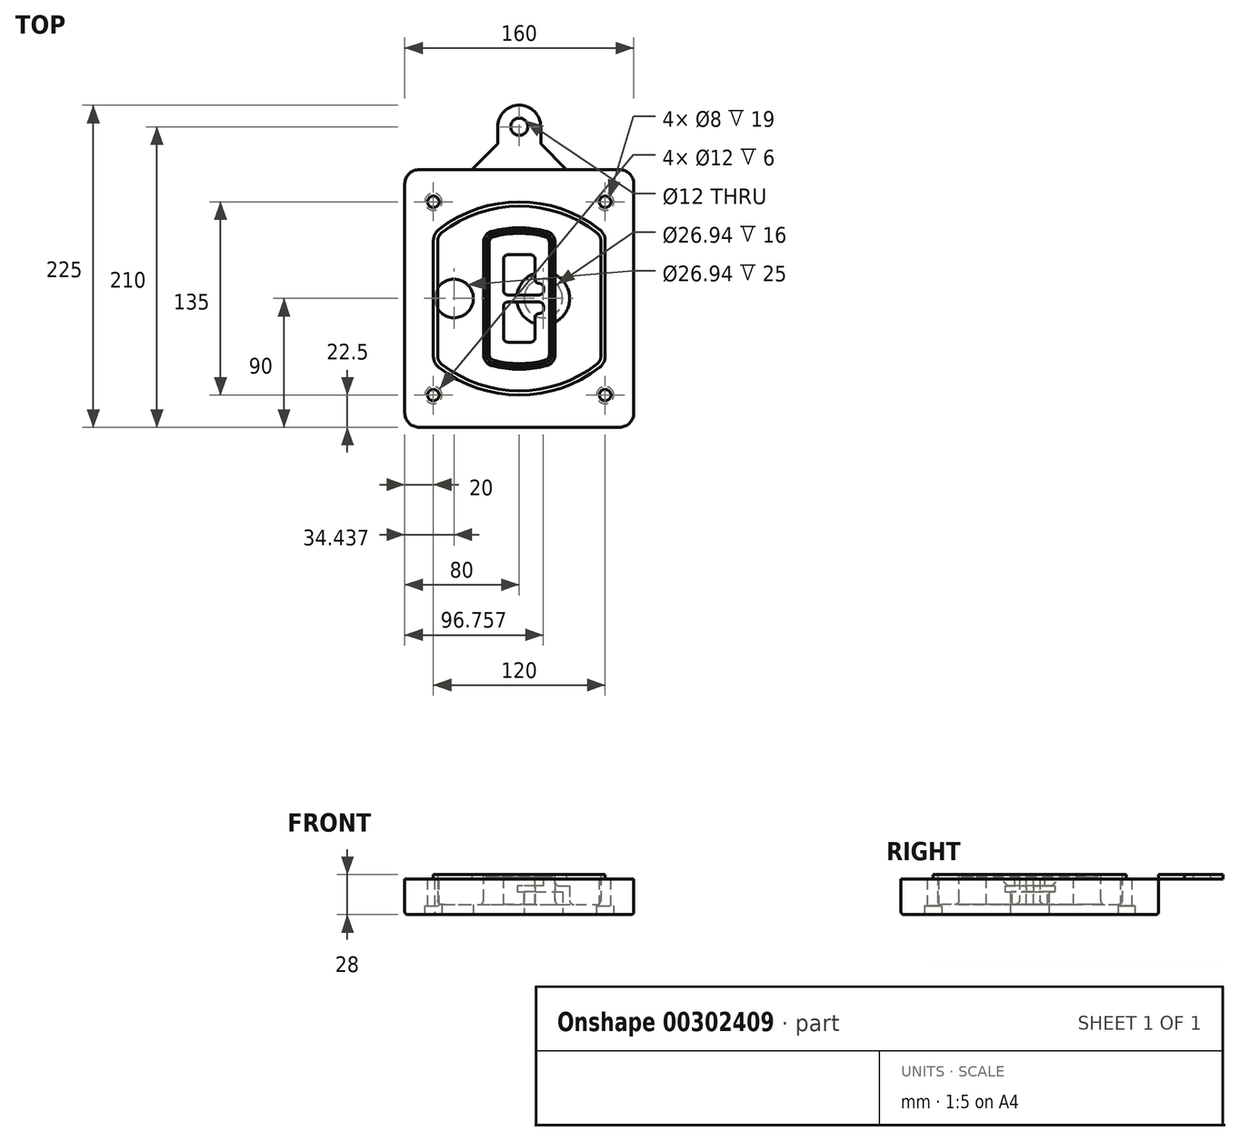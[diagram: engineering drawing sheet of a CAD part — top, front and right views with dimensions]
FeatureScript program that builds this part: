
annotation { "Feature Type Name" : "Feature", "Feature Type Description" : "" }
export const myFeature = defineFeature(function(context is Context, id is Id, definition is map)
    precondition{}
    {
        {
            var Q0;
            Q0=qCreatedBy(makeId("Top.planeOp"),FACE);
            var sketch = newSketch(context, id + "F0", { "sketchPlane" : qUnion([Q0])});
            skPoint(sketch, "E0.rect.middle", {"position": v(0, 0) * mm});
            skLineSegment(sketch, "E1.bottom", {"start": v(-70, -90) * mm, "end": v(70, -90) * mm});
            skLineSegment(sketch, "E1.top", {"start": v(-70, 90) * mm, "end": v(70, 90) * mm});
            skLineSegment(sketch, "E1.left", {"start": v(-80, -80) * mm, "end": v(-80, 80) * mm});
            skLineSegment(sketch, "E1.right", {"start": v(80, -80) * mm, "end": v(80, 80) * mm});
            skLineSegment(sketch, "E2", {"start": v(-80, 90) * mm, "end": v(80, -90) * mm, "construction": true});
            skLineSegment(sketch, "E3", {"start": v(80, 90) * mm, "end": v(-80, -90) * mm, "construction": true});
            skCircle(sketch, "E4", {"center": v(-60, 67.5) * mm, "radius": 4 * mm});
            skCircle(sketch, "E5", {"center": v(60, 67.5) * mm, "radius": 4 * mm});
            skCircle(sketch, "E6", {"center": v(60, -67.5) * mm, "radius": 4 * mm});
            skCircle(sketch, "E7", {"center": v(-60, -67.5) * mm, "radius": 4 * mm});
            skLineSegment(sketch, "E8", {"start": v(-60, 67.5) * mm, "end": v(60, 67.5) * mm, "construction": true});
            skLineSegment(sketch, "E9", {"start": v(60, 67.5) * mm, "end": v(60, -67.5) * mm, "construction": true});
            skLineSegment(sketch, "E10", {"start": v(60, -67.5) * mm, "end": v(-60, -67.5) * mm, "construction": true});
            skLineSegment(sketch, "E11", {"start": v(-60, -67.5) * mm, "end": v(-60, 67.5) * mm, "construction": true});
            skLineSegment(sketch, "E12", {"start": v(-60, 40.3) * mm, "end": v(-60, -40.3) * mm});
            skLineSegment(sketch, "E13", {"start": v(60, 40.3) * mm, "end": v(60, -40.3) * mm});
            skArc(sketch, "E14", {"start": v(56.15, 48.18) * mm, "mid": v(0, 67.5) * mm, "end": v(-56.15, 48.18) * mm});
            skArc(sketch, "E15", {"start": v(-56.15, -48.18) * mm, "mid": v(0, -67.5) * mm, "end": v(56.15, -48.18) * mm});
            skLineSegment(sketch, "E16", {"start": v(-60, 0) * mm, "end": v(60, 0) * mm, "construction": true});
            skPoint(sketch, "E17.visualSharp", {"position": v(-60, -45) * mm});
            skArc(sketch, "E17.filletArc", {"start": v(-60, -40.3) * mm, "mid": v(-58.99, -44.68) * mm, "end": v(-56.15, -48.18) * mm});
            skPoint(sketch, "E18.visualSharp", {"position": v(-60, 45) * mm});
            skArc(sketch, "E18.filletArc", {"start": v(-56.15, 48.18) * mm, "mid": v(-58.99, 44.68) * mm, "end": v(-60, 40.3) * mm});
            skPoint(sketch, "E19.visualSharp", {"position": v(60, 45) * mm});
            skArc(sketch, "E19.filletArc", {"start": v(60, 40.3) * mm, "mid": v(58.99, 44.68) * mm, "end": v(56.15, 48.18) * mm});
            skPoint(sketch, "E20.visualSharp", {"position": v(60, -45) * mm});
            skArc(sketch, "E20.filletArc", {"start": v(56.15, -48.18) * mm, "mid": v(58.99, -44.68) * mm, "end": v(60, -40.3) * mm});
            skPoint(sketch, "E21.visualSharp", {"position": v(-80, 90) * mm});
            skArc(sketch, "E21.filletArc", {"start": v(-70, 90) * mm, "mid": v(-77.07, 87.07) * mm, "end": v(-80, 80) * mm});
            skPoint(sketch, "E22.visualSharp", {"position": v(80, 90) * mm});
            skArc(sketch, "E22.filletArc", {"start": v(80, 80) * mm, "mid": v(77.07, 87.07) * mm, "end": v(70, 90) * mm});
            skPoint(sketch, "E23.visualSharp", {"position": v(80, -90) * mm});
            skArc(sketch, "E23.filletArc", {"start": v(70, -90) * mm, "mid": v(77.07, -87.07) * mm, "end": v(80, -80) * mm});
            skPoint(sketch, "E24.visualSharp", {"position": v(-80, -90) * mm});
            skArc(sketch, "E24.filletArc", {"start": v(-80, -80) * mm, "mid": v(-77.07, -87.07) * mm, "end": v(-70, -90) * mm});
            skArc(sketch, "E25.0", {"start": v(57, 40.3) * mm, "mid": v(56.3, 43.36) * mm, "end": v(54.3, 45.81) * mm});
            skLineSegment(sketch, "E25.1", {"start": v(57, 40.3) * mm, "end": v(57, -40.3) * mm});
            skArc(sketch, "E25.2", {"start": v(54.3, -45.81) * mm, "mid": v(56.3, -43.36) * mm, "end": v(57, -40.3) * mm});
            skArc(sketch, "E25.3", {"start": v(-54.3, -45.81) * mm, "mid": v(0, -64.5) * mm, "end": v(54.3, -45.81) * mm});
            skArc(sketch, "E25.4", {"start": v(-57, -40.3) * mm, "mid": v(-56.3, -43.36) * mm, "end": v(-54.3, -45.81) * mm});
            skArc(sketch, "E25.5", {"start": v(54.3, 45.81) * mm, "mid": v(0, 64.5) * mm, "end": v(-54.3, 45.81) * mm});
            skLineSegment(sketch, "E25.6", {"start": v(-57, 40.3) * mm, "end": v(-57, -40.3) * mm});
            skArc(sketch, "E25.7", {"start": v(-54.3, 45.81) * mm, "mid": v(-56.3, 43.36) * mm, "end": v(-57, 40.3) * mm});
            skArc(sketch, "E26.0", {"start": v(-58.62, 51.33) * mm, "mid": v(-62.58, 46.43) * mm, "end": v(-64, 40.3) * mm});
            skArc(sketch, "E26.1", {"start": v(58.62, 51.33) * mm, "mid": v(0, 71.5) * mm, "end": v(-58.62, 51.33) * mm});
            skArc(sketch, "E26.2", {"start": v(64, 40.3) * mm, "mid": v(62.58, 46.43) * mm, "end": v(58.62, 51.33) * mm});
            skLineSegment(sketch, "E26.3", {"start": v(64, 40.3) * mm, "end": v(64, -40.3) * mm});
            skArc(sketch, "E26.4", {"start": v(58.62, -51.33) * mm, "mid": v(62.58, -46.43) * mm, "end": v(64, -40.3) * mm});
            skLineSegment(sketch, "E26.5", {"start": v(-64, 40.3) * mm, "end": v(-64, -40.3) * mm});
            skArc(sketch, "E26.6", {"start": v(-58.62, -51.33) * mm, "mid": v(0, -71.5) * mm, "end": v(58.62, -51.33) * mm});
            skArc(sketch, "E26.7", {"start": v(-64, -40.3) * mm, "mid": v(-62.58, -46.43) * mm, "end": v(-58.62, -51.33) * mm});
            skSolve(sketch);
        }
        {
            var Q0;
            Q0=makeQuery(id+"F0.imprint","IMPRINT",FACE,{"disambiguationData":[TD([[makeQuery(id+"F0.imprint","IMPRINT",EDGE,{"derivedFrom":sQuery(id+"F0.wireOp",EDGE,"E1.bottom")}),1.0]])]});
            var Q1;
            Q1=makeQuery(id+"F0.imprint","IMPRINT",FACE,{"disambiguationData":[TD([[makeQuery(id+"F0.imprint","IMPRINT",EDGE,{"derivedFrom":sQuery(id+"F0.wireOp",EDGE,"E12")}),1.0]])]});
            var Q2;
            Q2=makeQuery(id+"F0.imprint","IMPRINT",FACE,{"disambiguationData":[TD([[makeQuery(id+"F0.imprint","IMPRINT",EDGE,{"derivedFrom":sQuery(id+"F0.wireOp",EDGE,"E25.0")}),1.0]])]});
            var Q3;
            Q3=makeQuery(id+"F0.imprint","IMPRINT",FACE,{"disambiguationData":[TD([[makeQuery(id+"F0.imprint","IMPRINT",EDGE,{"derivedFrom":sQuery(id+"F0.wireOp",EDGE,"E12")}),-1.0]])]});
            extrude(context, id + "F1", {"entities" : qUnion([Q0, Q1, Q2, Q3]), "oppositeDirection" : true, "depth" : 25 * mm});
        }
        {
            var Q0;
            Q0=makeQuery(id+"F0.imprint","IMPRINT",FACE,{"disambiguationData":[TD([[makeQuery(id+"F0.imprint","IMPRINT",EDGE,{"derivedFrom":sQuery(id+"F0.wireOp",EDGE,"E12")}),1.0]])]});
            extrude(context, id + "F2", {"entities" : qUnion([Q0]), "operationType" : NewBodyOperationType.ADD, "depth" : 3 * mm});
        }
        {
            var Q0;
            Q0=makeQuery(id+"F0.imprint","IMPRINT",FACE,{"disambiguationData":[TD([[makeQuery(id+"F0.imprint","IMPRINT",EDGE,{"derivedFrom":sQuery(id+"F0.wireOp",EDGE,"E25.0")}),1.0]])]});
            extrude(context, id + "F3", {"entities" : qUnion([Q0]), "operationType" : NewBodyOperationType.REMOVE, "oppositeDirection" : true, "depth" : 18 * mm});
        }
        {
            var Q0;
            Q0=makeQuery(id+"F2.opExtrude","CAP_FACE",FACE,{"disambiguationData":[OSD([sQuery(id+"F0.wireOp",EDGE,"E12"),sQuery(id+"F0.wireOp",EDGE,"E13"),sQuery(id+"F0.wireOp",EDGE,"E14"),sQuery(id+"F0.wireOp",EDGE,"E15"),sQuery(id+"F0.wireOp",EDGE,"E17.filletArc"),sQuery(id+"F0.wireOp",EDGE,"E18.filletArc"),sQuery(id+"F0.wireOp",EDGE,"E19.filletArc"),sQuery(id+"F0.wireOp",EDGE,"E20.filletArc"),sQuery(id+"F0.wireOp",EDGE,"E25.0"),sQuery(id+"F0.wireOp",EDGE,"E25.1"),sQuery(id+"F0.wireOp",EDGE,"E25.2"),sQuery(id+"F0.wireOp",EDGE,"E25.3"),sQuery(id+"F0.wireOp",EDGE,"E25.4"),sQuery(id+"F0.wireOp",EDGE,"E25.5"),sQuery(id+"F0.wireOp",EDGE,"E25.6"),sQuery(id+"F0.wireOp",EDGE,"E25.7")])],"isStart":false});
            var sketch = newSketch(context, id + "F4", { "sketchPlane" : qUnion([Q0])});
            skArc(sketch, "E27.0", {"start": v(-19.08, -46.97) * mm, "mid": v(0, -49.5) * mm, "end": v(19.08, -46.97) * mm});
            skArc(sketch, "E28.0", {"start": v(19.08, 46.97) * mm, "mid": v(0, 49.5) * mm, "end": v(-19.08, 46.97) * mm});
            skLineSegment(sketch, "E29", {"start": v(-25, 39.25) * mm, "end": v(-25, -39.25) * mm});
            skLineSegment(sketch, "E30", {"start": v(25, 39.25) * mm, "end": v(25, -39.25) * mm});
            skLineSegment(sketch, "E31", {"start": v(-25, 45.1) * mm, "end": v(25, 45.1) * mm, "construction": true});
            skLineSegment(sketch, "E32", {"start": v(-25, -45.1) * mm, "end": v(25, -45.1) * mm, "construction": true});
            skPoint(sketch, "E33.visualSharp", {"position": v(-25, 45.1) * mm});
            skArc(sketch, "E33.filletArc", {"start": v(-19.08, 46.97) * mm, "mid": v(-23.35, 44.11) * mm, "end": v(-25, 39.25) * mm});
            skPoint(sketch, "E34.visualSharp", {"position": v(25, 45.1) * mm});
            skArc(sketch, "E34.filletArc", {"start": v(25, 39.25) * mm, "mid": v(23.35, 44.11) * mm, "end": v(19.08, 46.97) * mm});
            skPoint(sketch, "E35.visualSharp", {"position": v(25, -45.1) * mm});
            skArc(sketch, "E35.filletArc", {"start": v(19.08, -46.97) * mm, "mid": v(23.35, -44.11) * mm, "end": v(25, -39.25) * mm});
            skPoint(sketch, "E36.visualSharp", {"position": v(-25, -45.1) * mm});
            skArc(sketch, "E36.filletArc", {"start": v(-25, -39.25) * mm, "mid": v(-23.35, -44.11) * mm, "end": v(-19.08, -46.97) * mm});
            skArc(sketch, "E37.0", {"start": v(54.3, 45.81) * mm, "mid": v(0, 64.5) * mm, "end": v(-54.3, 45.81) * mm});
            skArc(sketch, "E37.1", {"start": v(-54.3, 45.81) * mm, "mid": v(-56.3, 43.36) * mm, "end": v(-57, 40.3) * mm});
            skLineSegment(sketch, "E37.2", {"start": v(-57, 40.3) * mm, "end": v(-57, -40.3) * mm});
            skArc(sketch, "E37.3", {"start": v(-57, -40.3) * mm, "mid": v(-56.3, -43.36) * mm, "end": v(-54.3, -45.81) * mm});
            skArc(sketch, "E37.4", {"start": v(-54.3, -45.81) * mm, "mid": v(0, -64.5) * mm, "end": v(54.3, -45.81) * mm});
            skArc(sketch, "E37.5", {"start": v(54.3, -45.81) * mm, "mid": v(56.3, -43.36) * mm, "end": v(57, -40.3) * mm});
            skLineSegment(sketch, "E37.6", {"start": v(57, 40.3) * mm, "end": v(57, -40.3) * mm});
            skArc(sketch, "E37.7", {"start": v(57, 40.3) * mm, "mid": v(56.3, 43.36) * mm, "end": v(54.3, 45.81) * mm});
            skLineSegment(sketch, "E38.0", {"start": v(23, 39.25) * mm, "end": v(23, -39.25) * mm});
            skArc(sketch, "E38.1", {"start": v(18.56, -45.04) * mm, "mid": v(21.76, -42.9) * mm, "end": v(23, -39.25) * mm});
            skArc(sketch, "E38.2", {"start": v(-18.56, -45.04) * mm, "mid": v(0, -47.5) * mm, "end": v(18.56, -45.04) * mm});
            skArc(sketch, "E38.3", {"start": v(-23, -39.25) * mm, "mid": v(-21.76, -42.9) * mm, "end": v(-18.56, -45.04) * mm});
            skLineSegment(sketch, "E38.4", {"start": v(-23, 39.25) * mm, "end": v(-23, -39.25) * mm});
            skArc(sketch, "E38.5", {"start": v(23, 39.25) * mm, "mid": v(21.76, 42.9) * mm, "end": v(18.56, 45.04) * mm});
            skArc(sketch, "E38.6", {"start": v(-18.56, 45.04) * mm, "mid": v(-21.76, 42.9) * mm, "end": v(-23, 39.25) * mm});
            skArc(sketch, "E38.7", {"start": v(18.56, 45.04) * mm, "mid": v(0, 47.5) * mm, "end": v(-18.56, 45.04) * mm});
            skArc(sketch, "E39.0", {"start": v(21, 39.25) * mm, "mid": v(20.18, 41.68) * mm, "end": v(18.04, 43.1) * mm});
            skLineSegment(sketch, "E39.1", {"start": v(21, 39.25) * mm, "end": v(21, -39.25) * mm});
            skArc(sketch, "E39.2", {"start": v(18.04, -43.1) * mm, "mid": v(20.18, -41.68) * mm, "end": v(21, -39.25) * mm});
            skArc(sketch, "E39.3", {"start": v(-18.04, -43.1) * mm, "mid": v(0, -45.5) * mm, "end": v(18.04, -43.1) * mm});
            skArc(sketch, "E39.4", {"start": v(-21, -39.25) * mm, "mid": v(-20.18, -41.68) * mm, "end": v(-18.04, -43.1) * mm});
            skArc(sketch, "E39.5", {"start": v(18.04, 43.1) * mm, "mid": v(0, 45.5) * mm, "end": v(-18.04, 43.1) * mm});
            skLineSegment(sketch, "E39.6", {"start": v(-21, 39.25) * mm, "end": v(-21, -39.25) * mm});
            skArc(sketch, "E39.7", {"start": v(-18.04, 43.1) * mm, "mid": v(-20.18, 41.68) * mm, "end": v(-21, 39.25) * mm});
            skLineSegment(sketch, "E40", {"start": v(-25, 0) * mm, "end": v(25, 0) * mm, "construction": true});
            skLineSegment(sketch, "E41", {"start": v(-11, 5.5) * mm, "end": v(-11, 27.5) * mm});
            skLineSegment(sketch, "E42", {"start": v(-8, 30.5) * mm, "end": v(8, 30.5) * mm});
            skLineSegment(sketch, "E43", {"start": v(11, 27.5) * mm, "end": v(11, 13.5) * mm});
            skLineSegment(sketch, "E44", {"start": v(14, 10.5) * mm, "end": v(14, 10.5) * mm});
            skLineSegment(sketch, "E45", {"start": v(17, 7.5) * mm, "end": v(17, 5.5) * mm});
            skLineSegment(sketch, "E46", {"start": v(14, 2.5) * mm, "end": v(-8, 2.5) * mm});
            skPoint(sketch, "E47.visualSharp", {"position": v(-11, 30.5) * mm});
            skArc(sketch, "E47.filletArc", {"start": v(-8, 30.5) * mm, "mid": v(-10.12, 29.62) * mm, "end": v(-11, 27.5) * mm});
            skPoint(sketch, "E48.visualSharp", {"position": v(11, 30.5) * mm});
            skArc(sketch, "E48.filletArc", {"start": v(11, 27.5) * mm, "mid": v(10.12, 29.62) * mm, "end": v(8, 30.5) * mm});
            skPoint(sketch, "E49.visualSharp", {"position": v(11, 10.5) * mm});
            skArc(sketch, "E49.filletArc", {"start": v(11, 13.5) * mm, "mid": v(11.88, 11.38) * mm, "end": v(14, 10.5) * mm});
            skPoint(sketch, "E50.visualSharp", {"position": v(17, 10.5) * mm});
            skArc(sketch, "E50.filletArc", {"start": v(17, 7.5) * mm, "mid": v(16.12, 9.62) * mm, "end": v(14, 10.5) * mm});
            skPoint(sketch, "E51.visualSharp", {"position": v(17, 2.5) * mm});
            skArc(sketch, "E51.filletArc", {"start": v(14, 2.5) * mm, "mid": v(16.12, 3.38) * mm, "end": v(17, 5.5) * mm});
            skPoint(sketch, "E52.visualSharp", {"position": v(-11, 2.5) * mm});
            skArc(sketch, "E52.filletArc", {"start": v(-11, 5.5) * mm, "mid": v(-10.12, 3.38) * mm, "end": v(-8, 2.5) * mm});
            skLineSegment(sketch, "E53.0.MirrorCS", {"start": v(14, -2.5) * mm, "end": v(-8, -2.5) * mm});
            skArc(sketch, "E54.0.MirrorCS", {"start": v(-11, -5.5) * mm, "mid": v(-10.12, -3.38) * mm, "end": v(-8, -2.5) * mm});
            skLineSegment(sketch, "E55.0.MirrorCS", {"start": v(-11, -5.5) * mm, "end": v(-11, -27.5) * mm});
            skArc(sketch, "E56.0.MirrorCS", {"start": v(-8, -30.5) * mm, "mid": v(-10.12, -29.62) * mm, "end": v(-11, -27.5) * mm});
            skLineSegment(sketch, "E57.0.MirrorCS", {"start": v(-8, -30.5) * mm, "end": v(8, -30.5) * mm});
            skArc(sketch, "E58.0.MirrorCS", {"start": v(11, -27.5) * mm, "mid": v(10.12, -29.62) * mm, "end": v(8, -30.5) * mm});
            skLineSegment(sketch, "E59.0.MirrorCS", {"start": v(11, -27.5) * mm, "end": v(11, -13.5) * mm});
            skArc(sketch, "E60.0.MirrorCS", {"start": v(11, -13.5) * mm, "mid": v(11.88, -11.38) * mm, "end": v(14, -10.5) * mm});
            skArc(sketch, "E61.0.MirrorCS", {"start": v(17, -7.5) * mm, "mid": v(16.12, -9.62) * mm, "end": v(14, -10.5) * mm});
            skLineSegment(sketch, "E62.0.MirrorCS", {"start": v(17, -7.5) * mm, "end": v(17, -5.5) * mm});
            skArc(sketch, "E63.0.MirrorCS", {"start": v(14, -2.5) * mm, "mid": v(16.12, -3.38) * mm, "end": v(17, -5.5) * mm});
            skSolve(sketch);
        }
        {
            var Q0;
            Q0=makeQuery(id+"F4.imprint","IMPRINT",FACE,{"disambiguationData":[TD([[makeQuery(id+"F4.imprint","IMPRINT",EDGE,{"derivedFrom":sQuery(id+"F4.wireOp",EDGE,"E27.0")}),1.0]])]});
            var Q1;
            Q1=makeQuery(id+"F4.imprint","IMPRINT",FACE,{"disambiguationData":[TD([[makeQuery(id+"F4.imprint","IMPRINT",EDGE,{"derivedFrom":sQuery(id+"F4.wireOp",EDGE,"E38.0")}),-1.0]])]});
            var Q2;
            Q2=makeQuery(id+"F4.imprint","IMPRINT",FACE,{"disambiguationData":[TD([[makeQuery(id+"F4.imprint","IMPRINT",EDGE,{"derivedFrom":sQuery(id+"F4.wireOp",EDGE,"E39.0")}),1.0]])]});
            extrude(context, id + "F5", {"entities" : qUnion([Q0, Q1, Q2]), "operationType" : NewBodyOperationType.ADD, "endBound" : BoundingType.UP_TO_NEXT, "oppositeDirection" : true, "depth" : 25 * mm});
        }
        {
            var Q0;
            Q0=makeQuery(id+"F4.imprint","IMPRINT",FACE,{"disambiguationData":[TD([[makeQuery(id+"F4.imprint","IMPRINT",EDGE,{"derivedFrom":sQuery(id+"F4.wireOp",EDGE,"E38.0")}),-1.0]])]});
            extrude(context, id + "F6", {"entities" : qUnion([Q0]), "operationType" : NewBodyOperationType.REMOVE, "oppositeDirection" : true, "depth" : 2 * mm});
        }
        {
            var Q0;
            Q0=makeQuery(id+"F1.opExtrude","CAP_FACE",FACE,{"disambiguationData":[OSD([sQuery(id+"F0.wireOp",EDGE,"E1.bottom"),sQuery(id+"F0.wireOp",EDGE,"E1.top"),sQuery(id+"F0.wireOp",EDGE,"E1.left"),sQuery(id+"F0.wireOp",EDGE,"E1.right"),sQuery(id+"F0.wireOp",EDGE,"E4"),sQuery(id+"F0.wireOp",EDGE,"E5"),sQuery(id+"F0.wireOp",EDGE,"E6"),sQuery(id+"F0.wireOp",EDGE,"E7"),sQuery(id+"F0.wireOp",EDGE,"E21.filletArc"),sQuery(id+"F0.wireOp",EDGE,"E22.filletArc"),sQuery(id+"F0.wireOp",EDGE,"E23.filletArc"),sQuery(id+"F0.wireOp",EDGE,"E24.filletArc")])],"isStart":false});
            var sketch = newSketch(context, id + "F7", { "sketchPlane" : qUnion([Q0])});
            skCircle(sketch, "E64", {"center": v(16.76, 0) * mm, "radius": 13.47 * mm});
            skCircle(sketch, "E65", {"center": v(-45.56, 0) * mm, "radius": 13.47 * mm});
            skLineSegment(sketch, "E66", {"start": v(80, 0) * mm, "end": v(-80, 0) * mm});
            skCircle(sketch, "E67", {"center": v(16.76, 0) * mm, "radius": 18.47 * mm});
            skCircle(sketch, "E68", {"center": v(60, -67.5) * mm, "radius": 6 * mm});
            skCircle(sketch, "E69", {"center": v(-60, -67.5) * mm, "radius": 6 * mm});
            skCircle(sketch, "E70", {"center": v(-60, 67.5) * mm, "radius": 6 * mm});
            skCircle(sketch, "E71", {"center": v(60, 67.5) * mm, "radius": 6 * mm});
            skSolve(sketch);
        }
        {
            var Q0;
            {var subQ1=sQuery(id+"F7.wireOp",EDGE,"E66");var subQ4=sQuery(id+"F7.wireOp",EDGE,"E64");var subQ6=makeQuery(id+"F7.imprint","INTERSECT",VERTEX,{"disambiguationData":[OD(0.0)],"derivedFrom":[subQ4,subQ1]});Q0=makeQuery(id+"F7.imprint","IMPRINT",FACE,{"disambiguationData":[TD([[makeQuery(id+"F7.imprint","IMPRINT",EDGE,{"disambiguationData":[TD([[subQ6,-1.0]])],"derivedFrom":subQ4}),-1.0]])]});}
            var Q1;
            {var subQ0=sQuery(id+"F7.wireOp",EDGE,"E66");var subQ1=sQuery(id+"F7.wireOp",EDGE,"E64");var subQ3=makeQuery(id+"F7.imprint","INTERSECT",VERTEX,{"disambiguationData":[OD(0.0)],"derivedFrom":[subQ1,subQ0]});Q1=makeQuery(id+"F7.imprint","IMPRINT",FACE,{"disambiguationData":[TD([[makeQuery(id+"F7.imprint","IMPRINT",EDGE,{"disambiguationData":[TD([[subQ3,-1.0]])],"derivedFrom":subQ1}),1.0]])]});}
            var Q2;
            {var subQ0=sQuery(id+"F7.wireOp",EDGE,"E66");var subQ1=sQuery(id+"F7.wireOp",EDGE,"E64");var subQ3=makeQuery(id+"F7.imprint","INTERSECT",VERTEX,{"disambiguationData":[OD(0.0)],"derivedFrom":[subQ1,subQ0]});Q2=makeQuery(id+"F7.imprint","IMPRINT",FACE,{"disambiguationData":[TD([[makeQuery(id+"F7.imprint","IMPRINT",EDGE,{"disambiguationData":[TD([[subQ3,1.0]])],"derivedFrom":subQ1}),1.0]])]});}
            var Q3;
            {var subQ1=sQuery(id+"F7.wireOp",EDGE,"E66");var subQ4=sQuery(id+"F7.wireOp",EDGE,"E64");var subQ6=makeQuery(id+"F7.imprint","INTERSECT",VERTEX,{"disambiguationData":[OD(0.0)],"derivedFrom":[subQ4,subQ1]});Q3=makeQuery(id+"F7.imprint","IMPRINT",FACE,{"disambiguationData":[TD([[makeQuery(id+"F7.imprint","IMPRINT",EDGE,{"disambiguationData":[TD([[subQ6,1.0]])],"derivedFrom":subQ4}),-1.0]])]});}
            extrude(context, id + "F8", {"entities" : qUnion([Q0, Q1, Q2, Q3]), "operationType" : NewBodyOperationType.ADD, "oppositeDirection" : true, "depth" : 20 * mm});
        }
        {
            var Q0;
            {var subQ0=sQuery(id+"F7.wireOp",EDGE,"E66");var subQ1=sQuery(id+"F7.wireOp",EDGE,"E64");var subQ3=makeQuery(id+"F7.imprint","INTERSECT",VERTEX,{"disambiguationData":[OD(0.0)],"derivedFrom":[subQ1,subQ0]});Q0=makeQuery(id+"F7.imprint","IMPRINT",FACE,{"disambiguationData":[TD([[makeQuery(id+"F7.imprint","IMPRINT",EDGE,{"disambiguationData":[TD([[subQ3,-1.0]])],"derivedFrom":subQ1}),1.0]])]});}
            var Q1;
            {var subQ0=sQuery(id+"F7.wireOp",EDGE,"E66");var subQ1=sQuery(id+"F7.wireOp",EDGE,"E64");var subQ3=makeQuery(id+"F7.imprint","INTERSECT",VERTEX,{"disambiguationData":[OD(0.0)],"derivedFrom":[subQ1,subQ0]});Q1=makeQuery(id+"F7.imprint","IMPRINT",FACE,{"disambiguationData":[TD([[makeQuery(id+"F7.imprint","IMPRINT",EDGE,{"disambiguationData":[TD([[subQ3,1.0]])],"derivedFrom":subQ1}),1.0]])]});}
            extrude(context, id + "F9", {"entities" : qUnion([Q0, Q1]), "operationType" : NewBodyOperationType.REMOVE, "oppositeDirection" : true, "depth" : 16 * mm});
        }
        {
            var Q0;
            {var subQ0=sQuery(id+"F7.wireOp",EDGE,"E66");var subQ1=sQuery(id+"F7.wireOp",EDGE,"E65");var subQ3=makeQuery(id+"F7.imprint","INTERSECT",VERTEX,{"disambiguationData":[OD(0.0)],"derivedFrom":[subQ1,subQ0]});Q0=makeQuery(id+"F7.imprint","IMPRINT",FACE,{"disambiguationData":[TD([[makeQuery(id+"F7.imprint","IMPRINT",EDGE,{"disambiguationData":[TD([[subQ3,-1.0]])],"derivedFrom":subQ1}),1.0]])]});}
            var Q1;
            {var subQ0=sQuery(id+"F7.wireOp",EDGE,"E66");var subQ1=sQuery(id+"F7.wireOp",EDGE,"E65");var subQ3=makeQuery(id+"F7.imprint","INTERSECT",VERTEX,{"disambiguationData":[OD(0.0)],"derivedFrom":[subQ1,subQ0]});Q1=makeQuery(id+"F7.imprint","IMPRINT",FACE,{"disambiguationData":[TD([[makeQuery(id+"F7.imprint","IMPRINT",EDGE,{"disambiguationData":[TD([[subQ3,1.0]])],"derivedFrom":subQ1}),1.0]])]});}
            extrude(context, id + "F10", {"entities" : qUnion([Q0, Q1]), "operationType" : NewBodyOperationType.REMOVE, "oppositeDirection" : true, "depth" : 25 * mm});
        }
        {
            var Q0;
            Q0=makeQuery(id+"F7.imprint","IMPRINT",FACE,{"disambiguationData":[TD([[makeQuery(id+"F7.imprint","IMPRINT",EDGE,{"derivedFrom":sQuery(id+"F7.wireOp",EDGE,"E68")}),1.0]])]});
            var Q1;
            Q1=makeQuery(id+"F7.imprint","IMPRINT",FACE,{"disambiguationData":[TD([[makeQuery(id+"F7.imprint","IMPRINT",EDGE,{"derivedFrom":makeQuery(id+"F1.opExtrude","CAP_EDGE",EDGE,{"disambiguationData":[OSD([sQuery(id+"F0.wireOp",EDGE,"E5")])],"isStart":false})}),-1.0]])]});
            var Q2;
            Q2=makeQuery(id+"F7.imprint","IMPRINT",FACE,{"disambiguationData":[TD([[makeQuery(id+"F7.imprint","IMPRINT",EDGE,{"derivedFrom":sQuery(id+"F7.wireOp",EDGE,"E69")}),1.0]])]});
            var Q3;
            Q3=makeQuery(id+"F7.imprint","IMPRINT",FACE,{"disambiguationData":[TD([[makeQuery(id+"F7.imprint","IMPRINT",EDGE,{"derivedFrom":makeQuery(id+"F1.opExtrude","CAP_EDGE",EDGE,{"disambiguationData":[OSD([sQuery(id+"F0.wireOp",EDGE,"E4")])],"isStart":false})}),-1.0]])]});
            var Q4;
            Q4=makeQuery(id+"F7.imprint","IMPRINT",FACE,{"disambiguationData":[TD([[makeQuery(id+"F7.imprint","IMPRINT",EDGE,{"derivedFrom":sQuery(id+"F7.wireOp",EDGE,"E70")}),1.0]])]});
            var Q5;
            Q5=makeQuery(id+"F7.imprint","IMPRINT",FACE,{"disambiguationData":[TD([[makeQuery(id+"F7.imprint","IMPRINT",EDGE,{"derivedFrom":makeQuery(id+"F1.opExtrude","CAP_EDGE",EDGE,{"disambiguationData":[OSD([sQuery(id+"F0.wireOp",EDGE,"E7")])],"isStart":false})}),-1.0]])]});
            var Q6;
            Q6=makeQuery(id+"F7.imprint","IMPRINT",FACE,{"disambiguationData":[TD([[makeQuery(id+"F7.imprint","IMPRINT",EDGE,{"derivedFrom":sQuery(id+"F7.wireOp",EDGE,"E71")}),1.0]])]});
            var Q7;
            Q7=makeQuery(id+"F7.imprint","IMPRINT",FACE,{"disambiguationData":[TD([[makeQuery(id+"F7.imprint","IMPRINT",EDGE,{"derivedFrom":makeQuery(id+"F1.opExtrude","CAP_EDGE",EDGE,{"disambiguationData":[OSD([sQuery(id+"F0.wireOp",EDGE,"E6")])],"isStart":false})}),-1.0]])]});
            extrude(context, id + "F11", {"entities" : qUnion([Q0, Q1, Q2, Q3, Q4, Q5, Q6, Q7]), "operationType" : NewBodyOperationType.REMOVE, "oppositeDirection" : true, "depth" : 6 * mm});
        }
        {
            var Q0;
            Q0=makeQuery(id+"F9.boolean.opBoolean","COPY",FACE,{"derivedFrom":makeQuery(id+"F9.opExtrude","CAP_FACE",FACE,{"disambiguationData":[OSD([sQuery(id+"F7.wireOp",EDGE,"E64")])],"isStart":false})});
            var sketch = newSketch(context, id + "F12", { "sketchPlane" : qUnion([Q0])});
            skArc(sketch, "E72.0", {"start": v(11, 17.55) * mm, "mid": v(2.57, 11.82) * mm, "end": v(-1.54, 2.5) * mm});
            skArc(sketch, "E72.1", {"start": v(-1.54, -2.5) * mm, "mid": v(2.57, -11.82) * mm, "end": v(11, -17.55) * mm});
            skLineSegment(sketch, "E73", {"start": v(-1.54, -2.5) * mm, "end": v(14, -2.5) * mm});
            skLineSegment(sketch, "E74.0", {"start": v(14, 2.5) * mm, "end": v(-1.54, 2.5) * mm});
            skArc(sketch, "E74.1", {"start": v(14, 2.5) * mm, "mid": v(16.12, 3.38) * mm, "end": v(17, 5.5) * mm});
            skLineSegment(sketch, "E74.2", {"start": v(17, 7.5) * mm, "end": v(17, 5.5) * mm});
            skArc(sketch, "E74.3", {"start": v(17, 7.5) * mm, "mid": v(16.12, 9.62) * mm, "end": v(14, 10.5) * mm});
            skArc(sketch, "E74.4", {"start": v(11, 13.5) * mm, "mid": v(11.88, 11.38) * mm, "end": v(14, 10.5) * mm});
            skLineSegment(sketch, "E74.5", {"start": v(11, 17.55) * mm, "end": v(11, 13.5) * mm});
            skLineSegment(sketch, "E74.7", {"start": v(14, -2.5) * mm, "end": v(-1.54, -2.5) * mm});
            skArc(sketch, "E74.8", {"start": v(14, -2.5) * mm, "mid": v(16.12, -3.38) * mm, "end": v(17, -5.5) * mm});
            skLineSegment(sketch, "E74.9", {"start": v(17, -7.5) * mm, "end": v(17, -5.5) * mm});
            skArc(sketch, "E74.10", {"start": v(17, -7.5) * mm, "mid": v(16.12, -9.62) * mm, "end": v(14, -10.5) * mm});
            skArc(sketch, "E74.11", {"start": v(11, -13.5) * mm, "mid": v(11.88, -11.38) * mm, "end": v(14, -10.5) * mm});
            skLineSegment(sketch, "E74.12", {"start": v(11, -17.55) * mm, "end": v(11, -13.5) * mm});
            skPoint(sketch, "E75.orphan", {"position": v(11, -27.5) * mm});
            skPoint(sketch, "E76.orphan", {"position": v(-8, -2.5) * mm});
            skPoint(sketch, "E77.orphan", {"position": v(-8, 2.5) * mm});
            skPoint(sketch, "E78.orphan", {"position": v(11, 27.5) * mm});
            skSolve(sketch);
        }
        {
            var Q0;
            {var subQ7=sQuery(id+"F12.wireOp",EDGE,"E72.0");var subQ14=sQuery(id+"F12.wireOp",EDGE,"E72.1");var subQ16=sQuery(id+"F12.wireOp",EDGE,"E74.1");var subQ18=sQuery(id+"F12.wireOp",EDGE,"E74.8");Q0=qUnion([makeQuery(id+"F12.imprint","IMPRINT",FACE,{"disambiguationData":[TD([[makeQuery(id+"F12.imprint","IMPRINT",EDGE,{"derivedFrom":subQ7}),1.0]])]}),makeQuery(id+"F12.imprint","IMPRINT",FACE,{"disambiguationData":[TD([[makeQuery(id+"F12.imprint","IMPRINT",EDGE,{"derivedFrom":subQ14}),1.0]])]}),makeQuery(id+"F12.imprint","IMPRINT",FACE,{"disambiguationData":[TD([[makeQuery(id+"F12.imprint","IMPRINT",EDGE,{"derivedFrom":subQ16}),1.0]])]}),makeQuery(id+"F12.imprint","IMPRINT",FACE,{"disambiguationData":[TD([[makeQuery(id+"F12.imprint","IMPRINT",EDGE,{"derivedFrom":subQ18}),-1.0]])]})]);}
            var Q1;
            Q1=makeQuery(id+"F5.boolean.opBoolean","SPLIT",FACE,{"disambiguationData":[TD([makeQuery(id+"F5.opExtrude","SWEPT_FACE",FACE,{"disambiguationData":[OSD([sQuery(id+"F4.wireOp",EDGE,"E41")])]})])],"derivedFrom":makeQuery(id+"F3.boolean.opBoolean","COPY",FACE,{"derivedFrom":makeQuery(id+"F3.opExtrude","CAP_FACE",FACE,{"disambiguationData":[OSD([sQuery(id+"F0.wireOp",EDGE,"E25.0"),sQuery(id+"F0.wireOp",EDGE,"E25.1"),sQuery(id+"F0.wireOp",EDGE,"E25.2"),sQuery(id+"F0.wireOp",EDGE,"E25.3"),sQuery(id+"F0.wireOp",EDGE,"E25.4"),sQuery(id+"F0.wireOp",EDGE,"E25.5"),sQuery(id+"F0.wireOp",EDGE,"E25.6"),sQuery(id+"F0.wireOp",EDGE,"E25.7")])],"isStart":false})})});
            extrude(context, id + "F13", {"entities" : qUnion([Q0]), "operationType" : NewBodyOperationType.REMOVE, "endBound" : BoundingType.UP_TO_SURFACE, "endBoundEntityFace" : qUnion([Q1]), "depth" : 25 * mm});
        }
        {
            var Q0;
            Q0=makeQuery(id+"F3.boolean.opBoolean","COPY",EDGE,{"derivedFrom":makeQuery(id+"F3.opExtrude","CAP_EDGE",EDGE,{"disambiguationData":[OSD([sQuery(id+"F0.wireOp",EDGE,"E25.6")])],"isStart":false})});
            var Q1;
            Q1=makeQuery(id+"F8.boolean.opBoolean","INTERSECT",EDGE,{"derivedFrom":[makeQuery(id+"F5.opExtrude","SWEPT_FACE",FACE,{"disambiguationData":[OSD([sQuery(id+"F4.wireOp",EDGE,"E30")])]}),makeQuery(id+"F8.opExtrude","CAP_FACE",FACE,{"disambiguationData":[OSD([sQuery(id+"F7.wireOp",EDGE,"E67")])],"isStart":false})]});
            var Q2;
            Q2=makeQuery(id+"F8.boolean.opBoolean","INTERSECT",EDGE,{"disambiguationData":[OD(1.0)],"derivedFrom":[makeQuery(id+"F5.opExtrude","SWEPT_FACE",FACE,{"disambiguationData":[OSD([sQuery(id+"F4.wireOp",EDGE,"E30")])]}),makeQuery(id+"F8.opExtrude","SWEPT_FACE",FACE,{"disambiguationData":[OSD([sQuery(id+"F7.wireOp",EDGE,"E67")])]})]});
            var Q3;
            {var subQ0=sQuery(id+"F4.wireOp",EDGE,"E30");Q3=makeQuery(id+"F8.boolean.opBoolean","SPLIT",EDGE,{"disambiguationData":[TD([makeQuery(id+"F5.opExtrude","SWEPT_FACE",FACE,{"disambiguationData":[OSD([sQuery(id+"F4.wireOp",EDGE,"E35.filletArc")])]})])],"derivedFrom":makeQuery(id+"F5.opExtrude","CAP_EDGE",EDGE,{"disambiguationData":[OSD([subQ0])],"isStart":false})});}
            var Q4;
            {var subQ0=sQuery(id+"F0.wireOp",EDGE,"E25.7");var subQ1=sQuery(id+"F0.wireOp",EDGE,"E25.1");var subQ2=sQuery(id+"F0.wireOp",EDGE,"E25.6");var subQ3=sQuery(id+"F0.wireOp",EDGE,"E25.5");var subQ4=sQuery(id+"F0.wireOp",EDGE,"E25.4");var subQ5=sQuery(id+"F0.wireOp",EDGE,"E25.0");var subQ6=sQuery(id+"F0.wireOp",EDGE,"E25.2");var subQ7=sQuery(id+"F0.wireOp",EDGE,"E25.3");Q4=makeQuery(id+"F8.boolean.opBoolean","INTERSECT",EDGE,{"derivedFrom":[makeQuery(id+"F5.boolean.opBoolean","SPLIT",FACE,{"disambiguationData":[TD([makeQuery(id+"F2.opExtrude","SWEPT_FACE",FACE,{"disambiguationData":[OSD([subQ5])]})])],"derivedFrom":makeQuery(id+"F3.boolean.opBoolean","COPY",FACE,{"derivedFrom":makeQuery(id+"F3.opExtrude","CAP_FACE",FACE,{"disambiguationData":[OSD([subQ5,subQ1,subQ6,subQ7,subQ4,subQ3,subQ2,subQ0])],"isStart":false})})}),makeQuery(id+"F8.opExtrude","SWEPT_FACE",FACE,{"disambiguationData":[OSD([sQuery(id+"F7.wireOp",EDGE,"E67")])]})]});}
            var Q5;
            Q5=makeQuery(id+"F8.boolean.opBoolean","INTERSECT",EDGE,{"disambiguationData":[OD(0.0)],"derivedFrom":[makeQuery(id+"F5.opExtrude","SWEPT_FACE",FACE,{"disambiguationData":[OSD([sQuery(id+"F4.wireOp",EDGE,"E30")])]}),makeQuery(id+"F8.opExtrude","SWEPT_FACE",FACE,{"disambiguationData":[OSD([sQuery(id+"F7.wireOp",EDGE,"E67")])]})]});
            fillet(context, id + "F14", {"entities" : qUnion([Q0, Q1, Q2, Q3, Q4, Q5]), "radius" : 3 * mm, "tangentPropagation" : true, "allowEdgeOverflow" : false});
        }
        {
            var Q0;
            Q0=makeQuery(id+"F1.opExtrude","CAP_EDGE",EDGE,{"disambiguationData":[OSD([sQuery(id+"F0.wireOp",EDGE,"E1.bottom")])],"isStart":false});
            fillet(context, id + "F15", {"entities" : qUnion([Q0]), "radius" : 2 * mm, "tangentPropagation" : true, "allowEdgeOverflow" : false});
        }
        {
            var Q0;
            {var subQ0=sQuery(id+"F0.wireOp",EDGE,"E21.filletArc");var subQ1=sQuery(id+"F0.wireOp",EDGE,"E7");var subQ2=sQuery(id+"F0.wireOp",EDGE,"E6");var subQ3=sQuery(id+"F0.wireOp",EDGE,"E5");var subQ4=sQuery(id+"F0.wireOp",EDGE,"E4");var subQ5=sQuery(id+"F0.wireOp",EDGE,"E22.filletArc");var subQ6=sQuery(id+"F0.wireOp",EDGE,"E1.bottom");var subQ7=sQuery(id+"F0.wireOp",EDGE,"E1.right");var subQ8=sQuery(id+"F0.wireOp",EDGE,"E1.top");var subQ9=sQuery(id+"F0.wireOp",EDGE,"E1.left");var subQ10=sQuery(id+"F0.wireOp",EDGE,"E23.filletArc");var subQ11=sQuery(id+"F0.wireOp",EDGE,"E24.filletArc");Q0=makeQuery(id+"F2.boolean.opBoolean","SPLIT",FACE,{"disambiguationData":[TD([makeQuery(id+"F1.opExtrude","SWEPT_FACE",FACE,{"disambiguationData":[OSD([subQ6])]})])],"derivedFrom":makeQuery(id+"F1.opExtrude","CAP_FACE",FACE,{"disambiguationData":[OSD([subQ6,subQ8,subQ9,subQ7,subQ4,subQ3,subQ2,subQ1,subQ0,subQ5,subQ10,subQ11])],"isStart":true})});}
            var sketch = newSketch(context, id + "F16", { "sketchPlane" : qUnion([Q0])});
            skLineSegment(sketch, "E79", {"start": v(0, 90) * mm, "end": v(0, 120) * mm, "construction": true});
            skCircle(sketch, "E80", {"center": v(0, 120) * mm, "radius": 6 * mm});
            skArc(sketch, "E81", {"start": v(15, 120) * mm, "mid": v(0, 135) * mm, "end": v(-15, 120) * mm});
            skLineSegment(sketch, "E82", {"start": v(-15, 120) * mm, "end": v(-15, 108) * mm});
            skLineSegment(sketch, "E83", {"start": v(-15, 108) * mm, "end": v(-33, 90) * mm});
            skLineSegment(sketch, "E84", {"start": v(15, 120) * mm, "end": v(15, 108) * mm});
            skLineSegment(sketch, "E85", {"start": v(15, 108) * mm, "end": v(33, 90) * mm});
            skLineSegment(sketch, "E86", {"start": v(-80, 0) * mm, "end": v(0, 0) * mm, "construction": true});
            skLineSegment(sketch, "E87", {"start": v(0, 0) * mm, "end": v(80, 0) * mm, "construction": true});
            skArc(sketch, "E88.MirrorCS", {"start": v(15, -120) * mm, "mid": v(0, -135) * mm, "end": v(-15, -120) * mm});
            skCircle(sketch, "E89.MirrorC", {"center": v(0, -120) * mm, "radius": 6 * mm});
            skLineSegment(sketch, "E90.MirrorCS", {"start": v(15, -120) * mm, "end": v(15, -108) * mm});
            skLineSegment(sketch, "E91.MirrorCS", {"start": v(-15, -120) * mm, "end": v(-15, -108) * mm});
            skLineSegment(sketch, "E92.MirrorCS", {"start": v(-15, -108) * mm, "end": v(-33, -90) * mm});
            skLineSegment(sketch, "E93.MirrorCS", {"start": v(15, -108) * mm, "end": v(33, -90) * mm});
            skLineSegment(sketch, "E94.MirrorCS", {"start": v(0, -90) * mm, "end": v(0, -120) * mm, "construction": true});
            skSolve(sketch);
        }
        {
            var Q0;
            Q0=makeQuery(id+"F16.imprint","IMPRINT",FACE,{"disambiguationData":[TD([[makeQuery(id+"F16.imprint","IMPRINT",EDGE,{"derivedFrom":sQuery(id+"F16.wireOp",EDGE,"E80")}),-1.0]])]});
            var Q1;
            Q1=makeQuery(id+"F16.imprint","IMPRINT",FACE,{"disambiguationData":[TD([[makeQuery(id+"F16.imprint","IMPRINT",EDGE,{"derivedFrom":sQuery(id+"F16.wireOp",EDGE,"E88.MirrorCS")}),-1.0]])]});
            var Q2;
            Q2=makeQuery(id+"F2.opExtrude","CAP_FACE",FACE,{"disambiguationData":[OSD([sQuery(id+"F0.wireOp",EDGE,"E12"),sQuery(id+"F0.wireOp",EDGE,"E13"),sQuery(id+"F0.wireOp",EDGE,"E14"),sQuery(id+"F0.wireOp",EDGE,"E15"),sQuery(id+"F0.wireOp",EDGE,"E17.filletArc"),sQuery(id+"F0.wireOp",EDGE,"E18.filletArc"),sQuery(id+"F0.wireOp",EDGE,"E19.filletArc"),sQuery(id+"F0.wireOp",EDGE,"E20.filletArc"),sQuery(id+"F0.wireOp",EDGE,"E25.0"),sQuery(id+"F0.wireOp",EDGE,"E25.1"),sQuery(id+"F0.wireOp",EDGE,"E25.2"),sQuery(id+"F0.wireOp",EDGE,"E25.3"),sQuery(id+"F0.wireOp",EDGE,"E25.4"),sQuery(id+"F0.wireOp",EDGE,"E25.5"),sQuery(id+"F0.wireOp",EDGE,"E25.6"),sQuery(id+"F0.wireOp",EDGE,"E25.7")])],"isStart":false});
            extrude(context, id + "F17", {"entities" : qUnion([Q0, Q1]), "endBound" : BoundingType.UP_TO_SURFACE, "endBoundEntityFace" : qUnion([Q2]), "depth" : 25 * mm});
        }
    });
